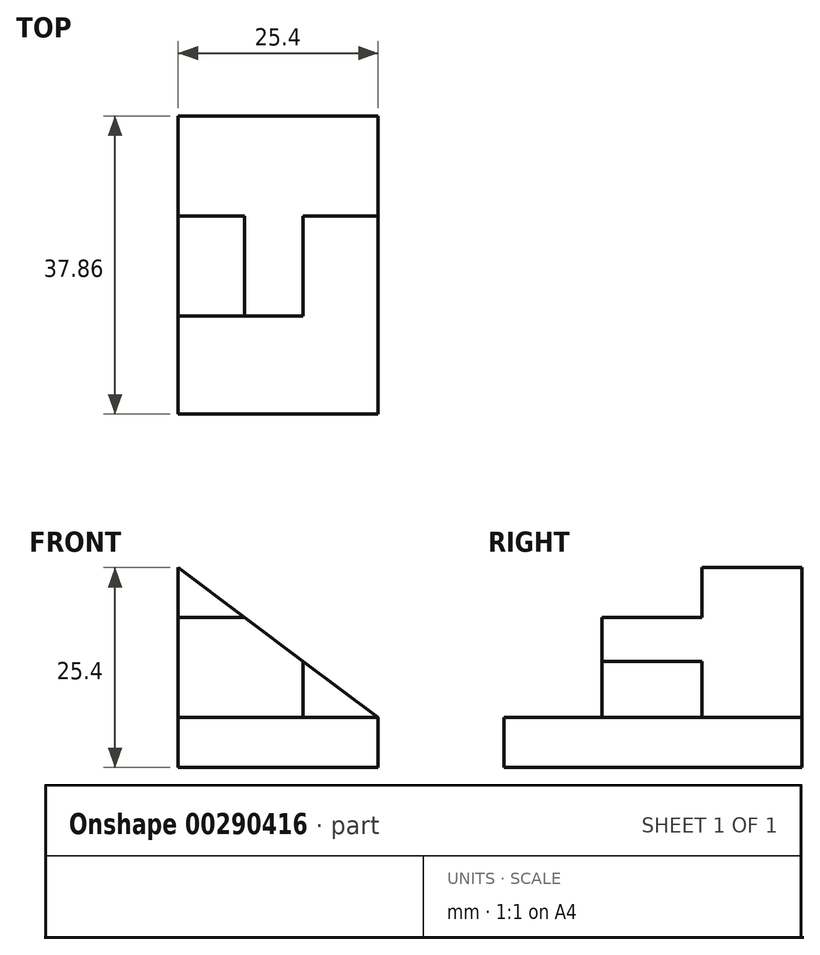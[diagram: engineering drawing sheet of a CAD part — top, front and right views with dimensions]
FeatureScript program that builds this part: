
annotation { "Feature Type Name" : "Feature", "Feature Type Description" : "" }
export const myFeature = defineFeature(function(context is Context, id is Id, definition is map)
    precondition{}
    {
        {
            var Q0;
            Q0=qCreatedBy(makeId("Front.planeOp"),FACE);
            var sketch = newSketch(context, id + "F0", { "sketchPlane" : qUnion([Q0])});
            skLineSegment(sketch, "E0", {"start": v(-35.78, 0) * mm, "end": v(-10.38, 0) * mm});
            skLineSegment(sketch, "E1", {"start": v(-10.38, 0) * mm, "end": v(-35.78, 19.05) * mm});
            skLineSegment(sketch, "E2", {"start": v(-35.78, 19.05) * mm, "end": v(-35.78, 0) * mm});
            skSolve(sketch);
        }
        {
            var Q0;
            Q0=makeQuery(id+"F0.imprint","IMPRINT",FACE,{"disambiguationData":[TD([[makeQuery(id+"F0.imprint","IMPRINT",EDGE,{"derivedFrom":sQuery(id+"F0.wireOp",EDGE,"E0")}),1.0]])]});
            extrude(context, id + "F1", {"entities" : qUnion([Q0]), "depth" : 25.4 * mm});
        }
        {
            var Q0;
            Q0=makeQuery(id+"F1.opExtrude","SWEPT_FACE",FACE,{"disambiguationData":[OSD([sQuery(id+"F0.wireOp",EDGE,"E0")])]});
            var sketch = newSketch(context, id + "F2", { "sketchPlane" : qUnion([Q0])});
            skLineSegment(sketch, "E3", {"start": v(-35.78, 0) * mm, "end": v(-35.78, 37.86) * mm});
            skLineSegment(sketch, "E4", {"start": v(-35.78, 37.86) * mm, "end": v(-10.38, 37.86) * mm});
            skLineSegment(sketch, "E5", {"start": v(-10.38, 37.86) * mm, "end": v(-10.38, 0) * mm});
            skLineSegment(sketch, "E6", {"start": v(-10.38, 0) * mm, "end": v(-35.78, 0) * mm});
            skSolve(sketch);
        }
        {
            var Q0;
            Q0 = qSketchRegion(id + "F2", true);
            extrude(context, id + "F3", {"entities" : qUnion([Q0]), "operationType" : NewBodyOperationType.ADD, "depth" : 6.35 * mm});
        }
        {
            var Q0;
            Q0=makeQuery(id+"F1.opExtrude","CAP_FACE",FACE,{"disambiguationData":[OSD([sQuery(id+"F0.wireOp",EDGE,"E0"),sQuery(id+"F0.wireOp",EDGE,"E1"),sQuery(id+"F0.wireOp",EDGE,"E2")])],"isStart":false});
            var sketch = newSketch(context, id + "F4", { "sketchPlane" : qUnion([Q0])});
            skLineSegment(sketch, "E7", {"start": v(-19.9, 7.14) * mm, "end": v(-19.9, 0) * mm});
            skLineSegment(sketch, "E8", {"start": v(-19.9, 0) * mm, "end": v(-10.38, 0) * mm});
            skLineSegment(sketch, "E9", {"start": v(-10.38, 0) * mm, "end": v(-19.9, 7.14) * mm});
            skSolve(sketch);
        }
        {
            var Q0;
            Q0 = qSketchRegion(id + "F4", true);
            extrude(context, id + "F5", {"entities" : qUnion([Q0]), "operationType" : NewBodyOperationType.REMOVE, "oppositeDirection" : true, "depth" : 12.7 * mm});
        }
        {
            var Q0;
            Q0=makeQuery(id+"F1.opExtrude","CAP_FACE",FACE,{"disambiguationData":[OSD([sQuery(id+"F0.wireOp",EDGE,"E0"),sQuery(id+"F0.wireOp",EDGE,"E1"),sQuery(id+"F0.wireOp",EDGE,"E2")])],"isStart":false});
            var sketch = newSketch(context, id + "F6", { "sketchPlane" : qUnion([Q0])});
            skLineSegment(sketch, "E10", {"start": v(-35.78, 12.7) * mm, "end": v(-27.31, 12.7) * mm});
            skLineSegment(sketch, "E11", {"start": v(-27.31, 12.7) * mm, "end": v(-35.78, 19.05) * mm});
            skLineSegment(sketch, "E12", {"start": v(-35.78, 19.05) * mm, "end": v(-35.78, 12.7) * mm});
            skSolve(sketch);
        }
        {
            var Q0;
            Q0 = qSketchRegion(id + "F6", true);
            extrude(context, id + "F7", {"entities" : qUnion([Q0]), "operationType" : NewBodyOperationType.REMOVE, "oppositeDirection" : true, "depth" : 12.7 * mm});
        }
    });
